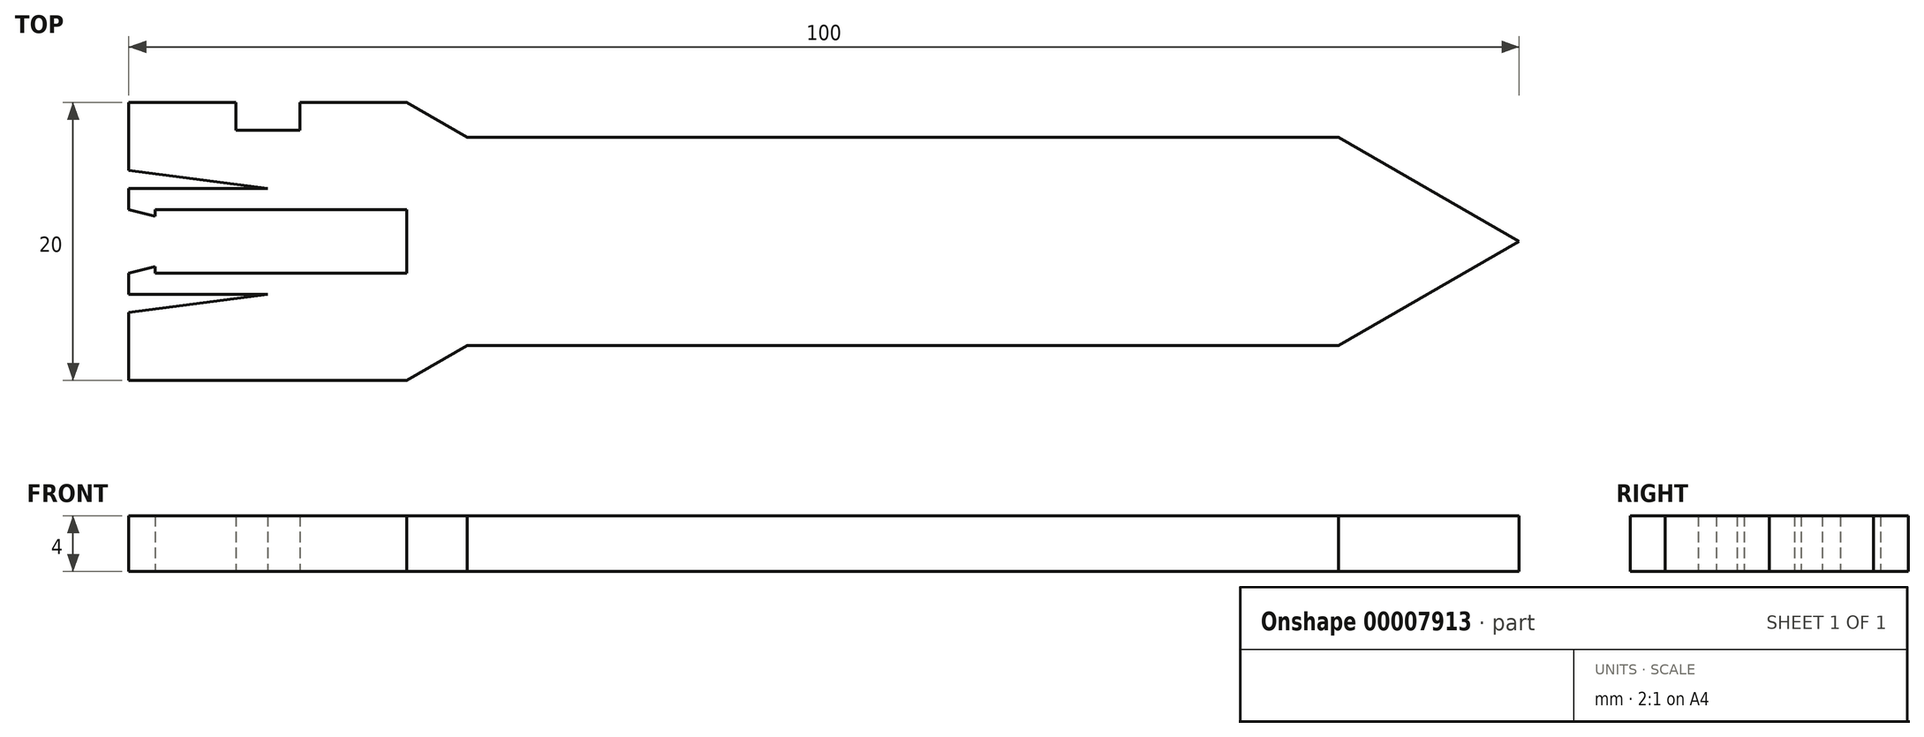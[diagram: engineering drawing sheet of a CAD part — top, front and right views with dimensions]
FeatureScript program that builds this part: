
annotation { "Feature Type Name" : "Feature", "Feature Type Description" : "" }
export const myFeature = defineFeature(function(context is Context, id is Id, definition is map)
    precondition{}
    {
        {
            var Q0;
            Q0=qCreatedBy(makeId("Top.planeOp"),FACE);
            var sketch = newSketch(context, id + "F0", { "sketchPlane" : qUnion([Q0])});
            skLineSegment(sketch, "E0.bottom", {"start": v(14.33, 7.5) * mm, "end": v(77, 7.5) * mm});
            skLineSegment(sketch, "E0.top", {"start": v(14.33, -7.5) * mm, "end": v(77, -7.5) * mm});
            skLineSegment(sketch, "E1.bottom", {"start": v(-10, 10) * mm, "end": v(-2.3, 10) * mm});
            skLineSegment(sketch, "E1.top", {"start": v(-10, -10) * mm, "end": v(10, -10) * mm});
            skLineSegment(sketch, "E1.left", {"start": v(-10, 10) * mm, "end": v(-10, 5.1) * mm});
            skLineSegment(sketch, "E2", {"start": v(10, 10) * mm, "end": v(14.33, 7.5) * mm});
            skLineSegment(sketch, "E3", {"start": v(14.33, -7.5) * mm, "end": v(10, -10) * mm});
            skLineSegment(sketch, "E4", {"start": v(77, -7.5) * mm, "end": v(90, 0) * mm});
            skLineSegment(sketch, "E5", {"start": v(90, 0) * mm, "end": v(77, 7.5) * mm});
            skLineSegment(sketch, "E6.bottom", {"start": v(-8.1, 2.3) * mm, "end": v(10, 2.3) * mm});
            skLineSegment(sketch, "E6.top", {"start": v(-8.1, -2.3) * mm, "end": v(10, -2.3) * mm});
            skLineSegment(sketch, "E6.right", {"start": v(10, 2.3) * mm, "end": v(10, -2.3) * mm});
            skLineSegment(sketch, "E7.trimOffspring", {"start": v(-10, -2.3) * mm, "end": v(-10, -3.8) * mm});
            skLineSegment(sketch, "E8.top", {"start": v(-2.3, 8) * mm, "end": v(2.3, 8) * mm});
            skLineSegment(sketch, "E8.left", {"start": v(-2.3, 10) * mm, "end": v(-2.3, 8) * mm});
            skLineSegment(sketch, "E8.right", {"start": v(2.3, 10) * mm, "end": v(2.3, 8) * mm});
            skLineSegment(sketch, "E9.trimOffspring", {"start": v(2.3, 10) * mm, "end": v(10, 10) * mm});
            skLineSegment(sketch, "E10", {"start": v(-10, -2.3) * mm, "end": v(-8.1, -1.8) * mm});
            skLineSegment(sketch, "E11", {"start": v(-8.1, -1.8) * mm, "end": v(-8.1, -2.3) * mm});
            skLineSegment(sketch, "E12", {"start": v(-10, -3.8) * mm, "end": v(0, -3.8) * mm});
            skLineSegment(sketch, "E13", {"start": v(0, -3.8) * mm, "end": v(-10, -5.1) * mm});
            skLineSegment(sketch, "E14.trimOffspring", {"start": v(-10, -5.1) * mm, "end": v(-10, -10) * mm});
            skLineSegment(sketch, "E15.0.MirrorCS", {"start": v(-8.1, 1.8) * mm, "end": v(-8.1, 2.3) * mm});
            skLineSegment(sketch, "E15.1.MirrorCS", {"start": v(0, 3.8) * mm, "end": v(-10, 5.1) * mm});
            skLineSegment(sketch, "E15.2.MirrorCS", {"start": v(-10, 3.8) * mm, "end": v(0, 3.8) * mm});
            skLineSegment(sketch, "E15.3.MirrorCS", {"start": v(-10, 2.3) * mm, "end": v(-8.1, 1.8) * mm});
            skLineSegment(sketch, "E15.4.MirrorCS", {"start": v(-10, 2.3) * mm, "end": v(-10, 3.8) * mm});
            skLineSegment(sketch, "E16.trimOffspring", {"start": v(-10, 3.8) * mm, "end": v(-10, 2.3) * mm});
            skLineSegment(sketch, "E17", {"start": v(10, 10) * mm, "end": v(10, 2.3) * mm, "construction": true});
            skSolve(sketch);
        }
        {
            var Q0;
            Q0=makeQuery(id+"F0.imprint","IMPRINT",FACE,{"disambiguationData":[TD([[makeQuery(id+"F0.imprint","IMPRINT",EDGE,{"derivedFrom":sQuery(id+"F0.wireOp",EDGE,"E0.bottom")}),-1.0]])]});
            extrude(context, id + "F1", {"entities" : qUnion([Q0]), "endBound" : BoundingType.SYMMETRIC, "depth" : 4 * mm});
        }
    });
